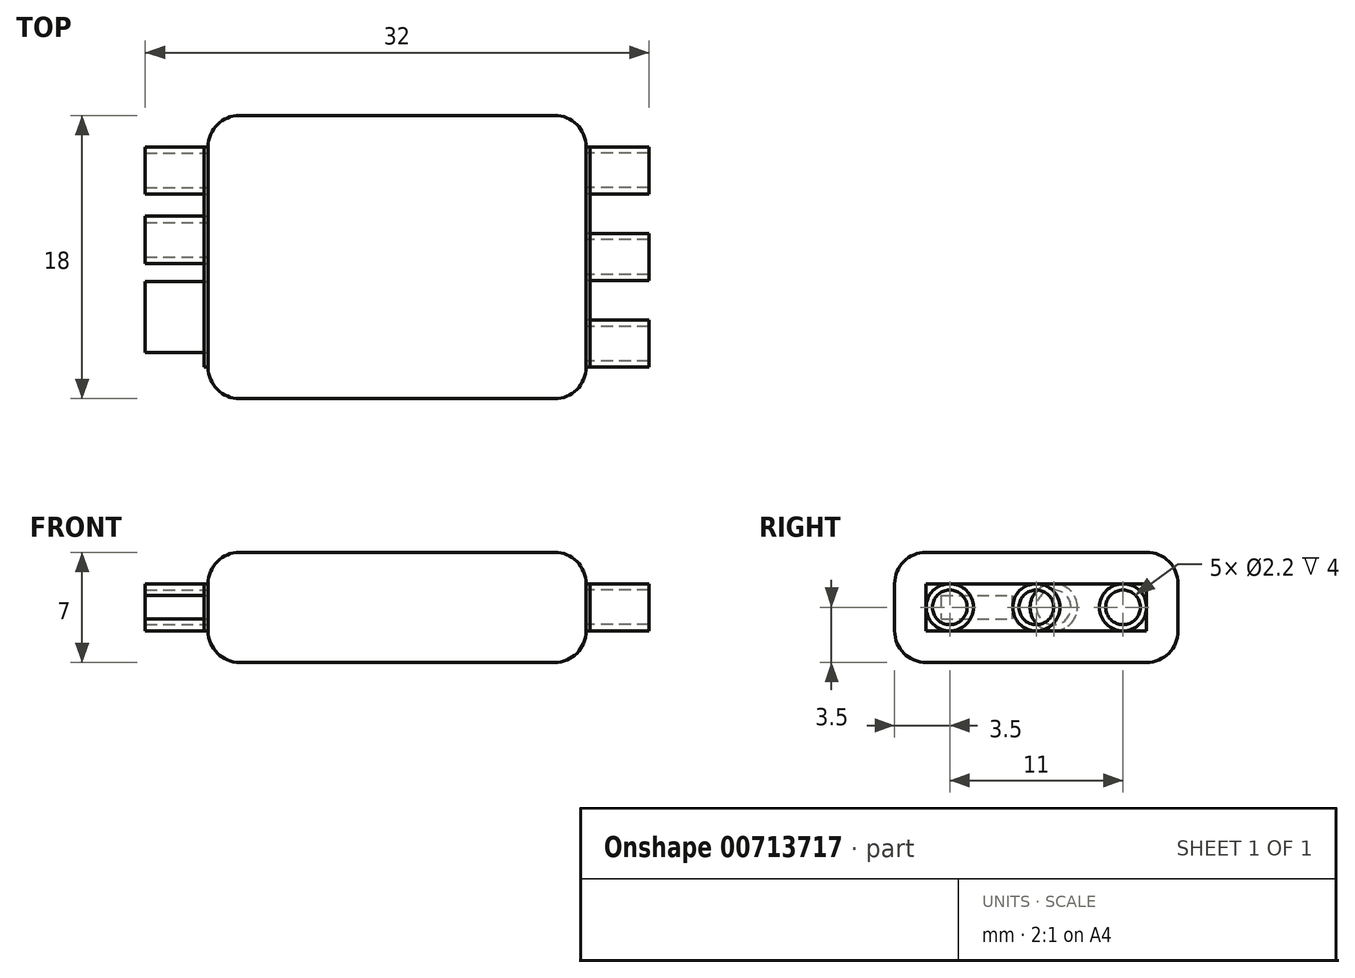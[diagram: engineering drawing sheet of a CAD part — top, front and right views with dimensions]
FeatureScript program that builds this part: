
annotation { "Feature Type Name" : "Feature", "Feature Type Description" : "" }
export const myFeature = defineFeature(function(context is Context, id is Id, definition is map)
    precondition{}
    {
        {
            var Q0;
            Q0=qCreatedBy(makeId("Top.planeOp"),FACE);
            var sketch = newSketch(context, id + "F0", { "sketchPlane" : qUnion([Q0])});
            skLineSegment(sketch, "E0.bottom", {"start": v(10, 9) * mm, "end": v(-10, 9) * mm});
            skLineSegment(sketch, "E0.top", {"start": v(10, -9) * mm, "end": v(-10, -9) * mm});
            skLineSegment(sketch, "E0.left", {"start": v(12, 7) * mm, "end": v(12, -7) * mm});
            skLineSegment(sketch, "E0.right", {"start": v(-12, 7) * mm, "end": v(-12, -7) * mm});
            skPoint(sketch, "E0.middle", {"position": v(0, 0) * mm});
            skPoint(sketch, "E1.visualSharp", {"position": v(-12, 9) * mm});
            skArc(sketch, "E1.filletArc", {"start": v(-10, 9) * mm, "mid": v(-11.41, 8.41) * mm, "end": v(-12, 7) * mm});
            skPoint(sketch, "E2.visualSharp", {"position": v(12, 9) * mm});
            skArc(sketch, "E2.filletArc", {"start": v(12, 7) * mm, "mid": v(11.41, 8.41) * mm, "end": v(10, 9) * mm});
            skPoint(sketch, "E3.visualSharp", {"position": v(12, -9) * mm});
            skArc(sketch, "E3.filletArc", {"start": v(10, -9) * mm, "mid": v(11.41, -8.41) * mm, "end": v(12, -7) * mm});
            skPoint(sketch, "E4.visualSharp", {"position": v(-12, -9) * mm});
            skArc(sketch, "E4.filletArc", {"start": v(-12, -7) * mm, "mid": v(-11.41, -8.41) * mm, "end": v(-10, -9) * mm});
            skSolve(sketch);
        }
        {
            var Q0;
            Q0=makeQuery(id+"F0.imprint","IMPRINT",FACE,{"disambiguationData":[TD([[makeQuery(id+"F0.imprint","IMPRINT",EDGE,{"derivedFrom":sQuery(id+"F0.wireOp",EDGE,"E0.bottom")}),1.0]])]});
            extrude(context, id + "F1", {"entities" : qUnion([Q0]), "depth" : 7 * mm});
        }
        {
            var Q0;
            Q0=makeQuery(id+"F1.opExtrude","CAP_FACE",FACE,{"disambiguationData":[OSD([sQuery(id+"F0.wireOp",EDGE,"E0.bottom"),sQuery(id+"F0.wireOp",EDGE,"E0.top"),sQuery(id+"F0.wireOp",EDGE,"E0.left"),sQuery(id+"F0.wireOp",EDGE,"E0.right"),sQuery(id+"F0.wireOp",EDGE,"E1.filletArc"),sQuery(id+"F0.wireOp",EDGE,"E2.filletArc"),sQuery(id+"F0.wireOp",EDGE,"E3.filletArc"),sQuery(id+"F0.wireOp",EDGE,"E4.filletArc")])],"isStart":false});
            var Q1;
            Q1=makeQuery(id+"F1.opExtrude","CAP_FACE",FACE,{"disambiguationData":[OSD([sQuery(id+"F0.wireOp",EDGE,"E0.bottom"),sQuery(id+"F0.wireOp",EDGE,"E0.top"),sQuery(id+"F0.wireOp",EDGE,"E0.left"),sQuery(id+"F0.wireOp",EDGE,"E0.right"),sQuery(id+"F0.wireOp",EDGE,"E1.filletArc"),sQuery(id+"F0.wireOp",EDGE,"E2.filletArc"),sQuery(id+"F0.wireOp",EDGE,"E3.filletArc"),sQuery(id+"F0.wireOp",EDGE,"E4.filletArc")])],"isStart":true});
            fillet(context, id + "F2", {"entities" : qUnion([Q0, Q1]), "radius" : 2 * mm, "tangentPropagation" : true, "allowEdgeOverflow" : false});
        }
        {
            var Q0;
            Q0=makeQuery(id+"F1.opExtrude","SWEPT_FACE",FACE,{"disambiguationData":[OSD([sQuery(id+"F0.wireOp",EDGE,"E0.left")])]});
            var sketch = newSketch(context, id + "F3", { "sketchPlane" : qUnion([Q0])});
            skLineSegment(sketch, "E5", {"start": v(-7, 3.5) * mm, "end": v(7, 3.5) * mm, "construction": true});
            skCircle(sketch, "E6", {"center": v(0, 3.5) * mm, "radius": 1.1 * mm});
            skCircle(sketch, "E7", {"center": v(0, 3.5) * mm, "radius": 1.5 * mm});
            skCircle(sketch, "E8", {"center": v(5.5, 3.5) * mm, "radius": 1.5 * mm});
            skCircle(sketch, "E9", {"center": v(5.5, 3.5) * mm, "radius": 1.1 * mm});
            skCircle(sketch, "E10", {"center": v(-5.5, 3.5) * mm, "radius": 1.5 * mm});
            skCircle(sketch, "E11", {"center": v(-5.5, 3.5) * mm, "radius": 1.1 * mm});
            skSolve(sketch);
        }
        {
            var Q0;
            Q0=makeQuery(id+"F3.imprint","IMPRINT",FACE,{"disambiguationData":[TD([[makeQuery(id+"F3.imprint","IMPRINT",EDGE,{"derivedFrom":sQuery(id+"F3.wireOp",EDGE,"E11")}),-1.0]])]});
            var Q1;
            Q1=makeQuery(id+"F3.imprint","IMPRINT",FACE,{"disambiguationData":[TD([[makeQuery(id+"F3.imprint","IMPRINT",EDGE,{"derivedFrom":sQuery(id+"F3.wireOp",EDGE,"E6")}),-1.0]])]});
            var Q2;
            Q2=makeQuery(id+"F3.imprint","IMPRINT",FACE,{"disambiguationData":[TD([[makeQuery(id+"F3.imprint","IMPRINT",EDGE,{"derivedFrom":sQuery(id+"F3.wireOp",EDGE,"E9")}),-1.0]])]});
            extrude(context, id + "F4", {"entities" : qUnion([Q0, Q1, Q2]), "depth" : 4 * mm});
        }
        {
            var Q0;
            Q0=makeQuery(id+"F1.opExtrude","SWEPT_FACE",FACE,{"disambiguationData":[OSD([sQuery(id+"F0.wireOp",EDGE,"E0.right")])]});
            var sketch = newSketch(context, id + "F5", { "sketchPlane" : qUnion([Q0])});
            skCircle(sketch, "E12.0", {"center": v(-5.5, 3.5) * mm, "radius": 1.5 * mm});
            skCircle(sketch, "E13.0", {"center": v(-5.5, 3.5) * mm, "radius": 1.1 * mm});
            skCircle(sketch, "E14", {"center": v(-1.1, 3.5) * mm, "radius": 1.5 * mm});
            skCircle(sketch, "E15", {"center": v(-1.1, 3.5) * mm, "radius": 1.1 * mm});
            skLineSegment(sketch, "E16.bottom", {"start": v(6.06, 4.25) * mm, "end": v(1.56, 4.25) * mm});
            skLineSegment(sketch, "E16.top", {"start": v(6.06, 2.75) * mm, "end": v(1.56, 2.75) * mm});
            skLineSegment(sketch, "E16.left", {"start": v(6.06, 4.25) * mm, "end": v(6.06, 2.75) * mm});
            skLineSegment(sketch, "E16.right", {"start": v(1.56, 4.25) * mm, "end": v(1.56, 2.75) * mm});
            skPoint(sketch, "E16.middle", {"position": v(3.8, 3.5) * mm});
            skPoint(sketch, "E16.middle.positionSnap0", {"position": v(7, 3.5) * mm});
            skPoint(sketch, "E16.centerSnap0", {"position": v(7, 3.5) * mm});
            skSolve(sketch);
        }
        {
            var Q0;
            Q0=qSketchRegion(id+"F5",true);
            extrude(context, id + "F6", {"entities" : qUnion([Q0]), "depth" : 4 * mm});
        }
        {
            var Q0;
            Q0=makeQuery(id+"F1.opExtrude","SWEPT_FACE",FACE,{"disambiguationData":[OSD([sQuery(id+"F0.wireOp",EDGE,"E0.left")])]});
            var sketch = newSketch(context, id + "F7", { "sketchPlane" : qUnion([Q0])});
            skLineSegment(sketch, "E17.bottom", {"start": v(-7, 5) * mm, "end": v(7, 5) * mm});
            skLineSegment(sketch, "E17.top", {"start": v(-7, 2) * mm, "end": v(7, 2) * mm});
            skLineSegment(sketch, "E17.left", {"start": v(-7, 5) * mm, "end": v(-7, 2) * mm});
            skLineSegment(sketch, "E17.right", {"start": v(7, 5) * mm, "end": v(7, 2) * mm});
            skSolve(sketch);
        }
        {
            var Q0;
            Q0=qSketchRegion(id+"F7",true);
            extrude(context, id + "F8", {"entities" : qUnion([Q0]), "depth" : .25 * mm});
        }
        {
            var Q0;
            Q0=makeQuery(id+"F1.opExtrude","SWEPT_FACE",FACE,{"disambiguationData":[OSD([sQuery(id+"F0.wireOp",EDGE,"E0.right")])]});
            var sketch = newSketch(context, id + "F9", { "sketchPlane" : qUnion([Q0])});
            skLineSegment(sketch, "E18.bottom", {"start": v(-7, 5) * mm, "end": v(7, 5) * mm});
            skLineSegment(sketch, "E18.top", {"start": v(-7, 2) * mm, "end": v(7, 2) * mm});
            skLineSegment(sketch, "E18.left", {"start": v(-7, 5) * mm, "end": v(-7, 2) * mm});
            skLineSegment(sketch, "E18.right", {"start": v(7, 5) * mm, "end": v(7, 2) * mm});
            skSolve(sketch);
        }
        {
            var Q0;
            Q0=makeQuery(id+"F9.imprint","IMPRINT",FACE,{"disambiguationData":[TD([[makeQuery(id+"F9.imprint","IMPRINT",EDGE,{"derivedFrom":sQuery(id+"F9.wireOp",EDGE,"E18.bottom")}),1.0]])]});
            extrude(context, id + "F10", {"entities" : qUnion([Q0]), "depth" : .25 * mm});
        }
    });
